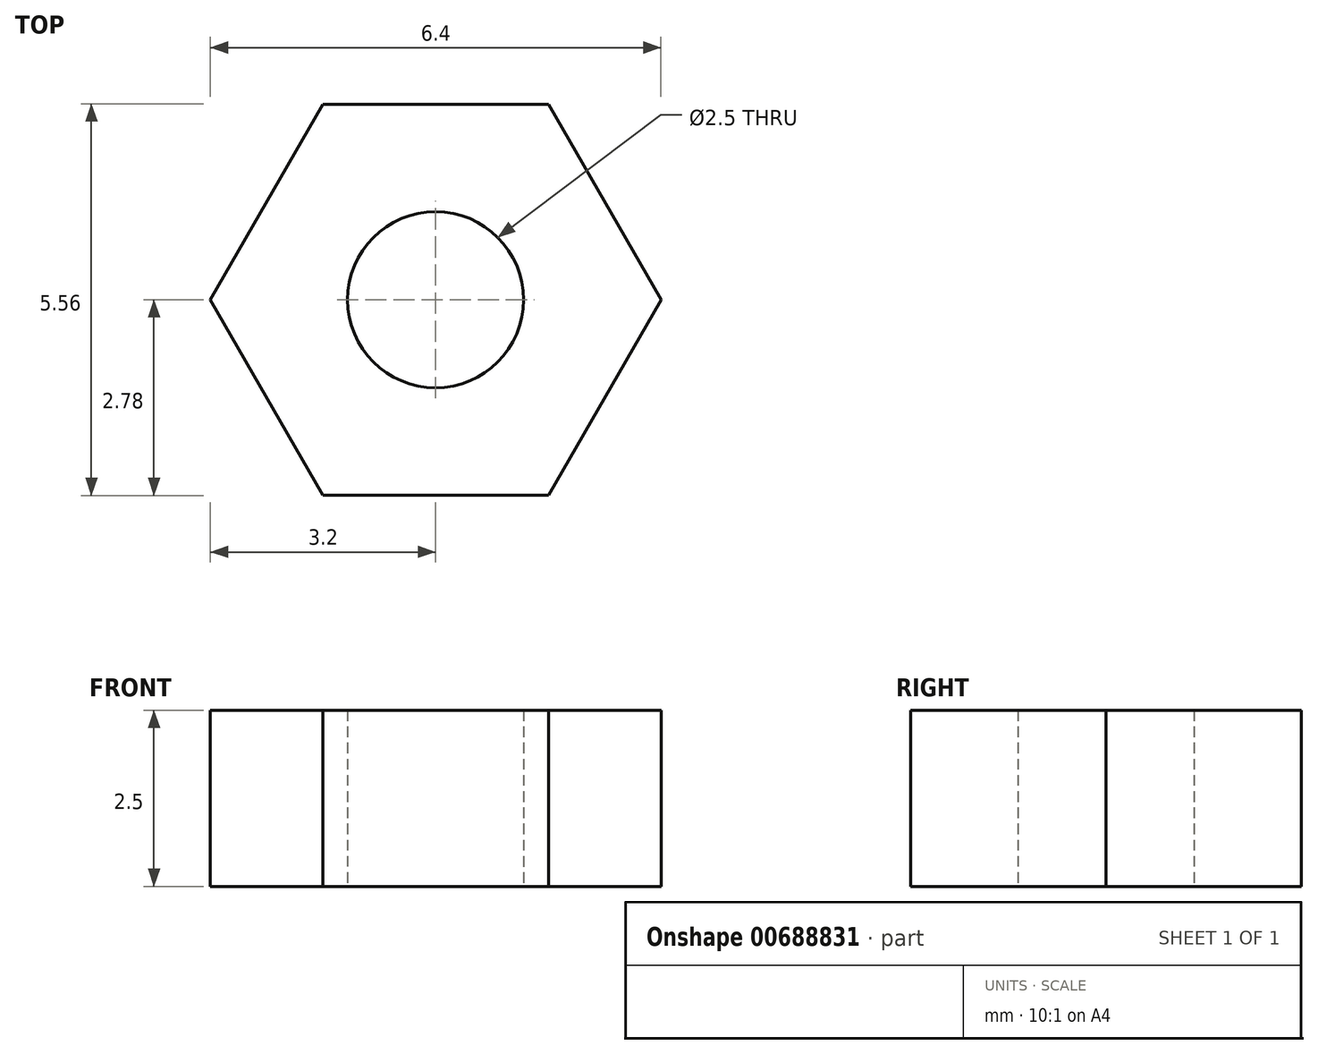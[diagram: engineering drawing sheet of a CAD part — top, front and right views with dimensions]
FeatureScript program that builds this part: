
annotation { "Feature Type Name" : "Feature", "Feature Type Description" : "" }
export const myFeature = defineFeature(function(context is Context, id is Id, definition is map)
    precondition{}
    {
        {
            var Q0;
            Q0=qCreatedBy(makeId("Top.planeOp"),FACE);
            var sketch = newSketch(context, id + "F0", { "sketchPlane" : qUnion([Q0])});
            skCircle(sketch, "E0.cCircle", {"center": v(0, 0) * mm, "radius": 2.78 * mm, "construction": true});
            skLineSegment(sketch, "E0.0", {"start": v(-3.2, 0) * mm, "end": v(-1.6, 2.77) * mm});
            skLineSegment(sketch, "E0.1", {"start": v(-1.6, 2.77) * mm, "end": v(1.6, 2.77) * mm});
            skLineSegment(sketch, "E0.2", {"start": v(1.6, 2.78) * mm, "end": v(3.2, 0) * mm});
            skLineSegment(sketch, "E0.3", {"start": v(3.2, 0) * mm, "end": v(1.6, -2.78) * mm});
            skLineSegment(sketch, "E0.4", {"start": v(1.6, -2.77) * mm, "end": v(-1.6, -2.77) * mm});
            skLineSegment(sketch, "E0.5", {"start": v(-1.6, -2.78) * mm, "end": v(-3.2, 0) * mm});
            skPoint(sketch, "E0.0.midPoint", {"position": v(-2.4, 1.39) * mm});
            skCircle(sketch, "E1", {"center": v(0, 0) * mm, "radius": 1.25 * mm});
            skSolve(sketch);
        }
        {
            var Q0;
            Q0=makeQuery(id+"F0.imprint","IMPRINT",FACE,{"disambiguationData":[TD([[makeQuery(id+"F0.imprint","IMPRINT",EDGE,{"derivedFrom":sQuery(id+"F0.wireOp",EDGE,"E0.0")}),-1.0]])]});
            extrude(context, id + "F1", {"entities" : qUnion([Q0]), "depth" : 2.5 * mm, "offsetDistance" : 25 * mm});
        }
    });
